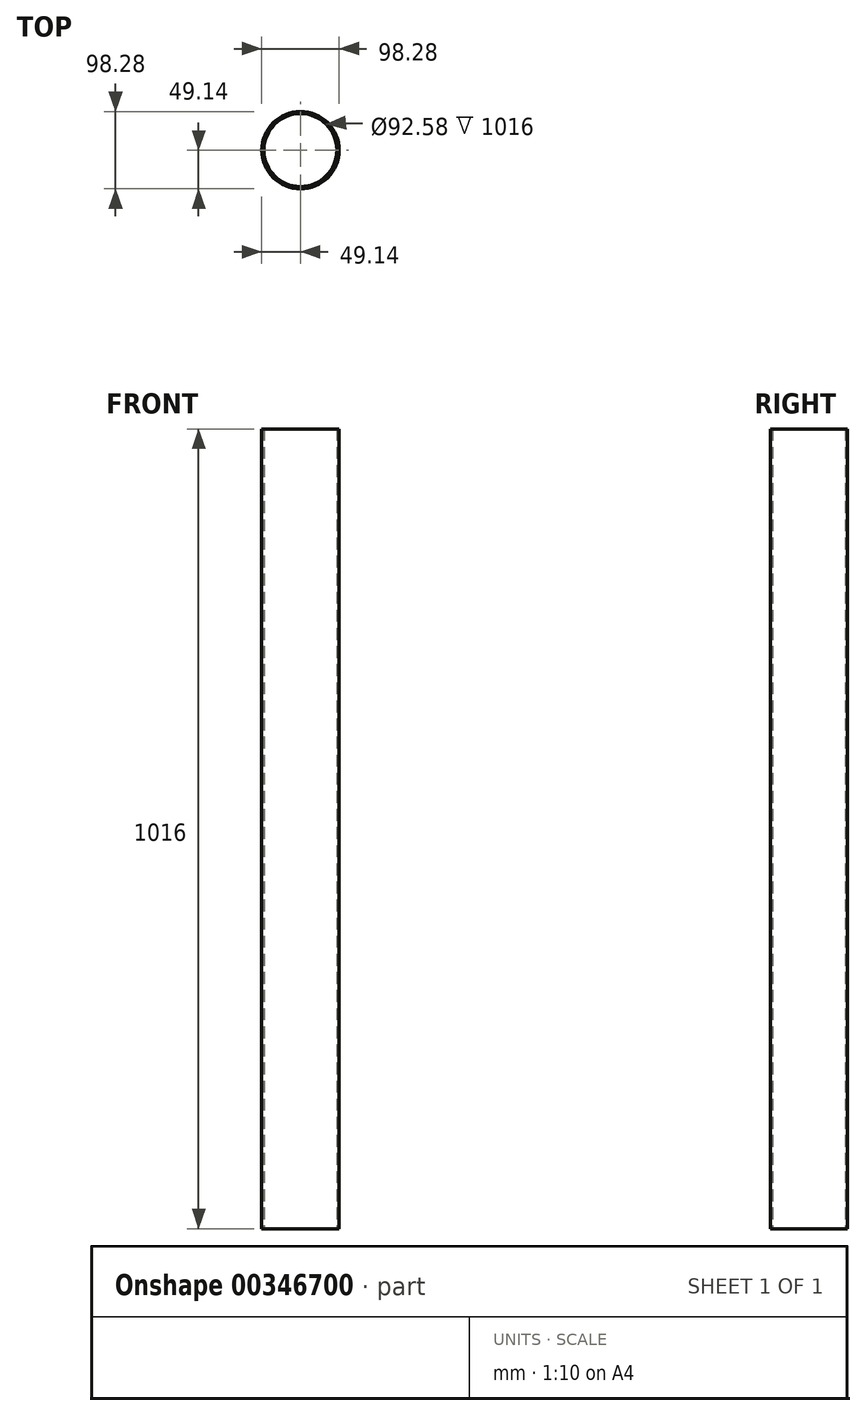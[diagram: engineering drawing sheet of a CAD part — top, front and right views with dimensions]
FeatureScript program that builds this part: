
annotation { "Feature Type Name" : "Feature", "Feature Type Description" : "" }
export const myFeature = defineFeature(function(context is Context, id is Id, definition is map)
    precondition{}
    {
        {
            var Q0;
            Q0=qCreatedBy(makeId("Top.planeOp"),FACE);
            var sketch = newSketch(context, id + "F0", { "sketchPlane" : qUnion([Q0])});
            skCircle(sketch, "E0", {"center": v(0, 0) * mm, "radius": 46.3 * mm});
            skCircle(sketch, "E1", {"center": v(0, 0) * mm, "radius": 49.14 * mm});
            skSolve(sketch);
        }
        {
            var Q0;
            Q0 = qSketchRegion(id + "F0", true);
            extrude(context, id + "F1", {"entities" : qUnion([Q0]), "depth" : 1016 * mm});
        }
    });
